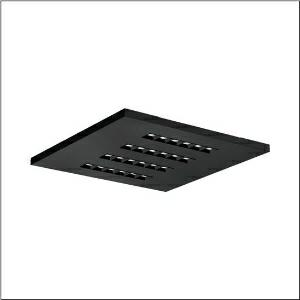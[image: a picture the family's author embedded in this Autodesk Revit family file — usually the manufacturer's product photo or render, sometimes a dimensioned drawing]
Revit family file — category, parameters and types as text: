
# Revit family: silica_21_square_51mx6kdu44b
name_source: partatom
category: Lighting Fixtures
units: mm (PartAtom-declared; Revit-internal decimal feet)

## family parameters
Cut with Voids When Loaded = No
Host = Face
Light Source = No
Part Type = Normal
Room Calculation Point = No
Round Connector Dimension = Use Diameter
Shared = No

## types (1)
- --- (1 x LED, 4600 lm, 29.6 W, 4000K)
    Apparent Load = 30 VA
    CIE Flux Codes = 86 100 100 100 100
    Color Rendering = 80
    Color Temperature = 4000K
    Default Elevation = 1800 mm
    Description = Silica 21 Square, office luminaire, primary light control with lens, of PMMA, primary anti-glare with reflector, of PC, black, CAT 2 (L<= 3000cd/m²), light emission: direct distribution, primary light characteristic: symmetric, installation type: lay-in mounting, LED, rated luminous flux: 4.600lm, luminous efficacy: 155lm/W, light colour: 840, colour temperature: 4000K, control gear: DALI 2, with terminal, 5-pole, mains connection: 220..240V, AC, 50/60Hz, rated input power: 29.6W, luminaire housing, of aluminium, matt jet black (RAL 9005), module: M625, length: 622mm, width: 622mm, height: 33mm, protection rating (complete): IP20, insulation class (complete): insulation class I (protective earthing), certification: CE, ENEC, VDE, permissible operating ambient temperature: -20..+40°C, standard: EN 50419, packaging unit: 1 piece
    Height = 0 mm  [stored 0 ft]
    Lamp = 1 x LED
    Lamp Light Flux = 4600 lm
    Lamp Power = 29.6 W
    Lamp count = 1
    Length = 622 mm
    Luminous efficacy = 155 lm/W
    Manufacturer = Siteco
    ModVariant = No
    Model = 51MX6KDU44B
    Mounting Place = Ceiling
    Mounting Type = Recessed
    Number of Poles = 1
    OnlyDefault = Yes
    Power Factor = 1
    Product Name = Silica 21 Square
    Product group = office luminaire | ceiling recessed
    ProductGroupID = 400
    Protection Class = Protection class I
    Protection Degree = IP 20
    RLX_Detail_Level = 1
    RLX_Emergency_Light_Flux = 0 lm
    RLX_Emergency_Type = 0
    RLX_Emergency_Type_DB = No
    RlxData = <blob elided: 25057 chars, md5=39d4d135>
    Socket = socket
    Standby Power = 0 W
    System Light Flux = 4600 lm
    System Power = 30 W
    Type Comments = factory setting: luminous flux: 100 % | dim-lin: 254 | 399 mA
    Type Image = l_1275204.jpg
    URL = http://relux.com
    VarID = @adj_088911
    Voltage = 0 V
    Weight = 0.00 kg
    Width = 622 mm

note: [stored X ft] marks values corroborated as IEEE doubles in the binary element streams (Revit-internal decimal feet)

## geometry (parser evidence)
native form markers: Blend x4, Sweep x10
no freeform markers — native parametric forms only
